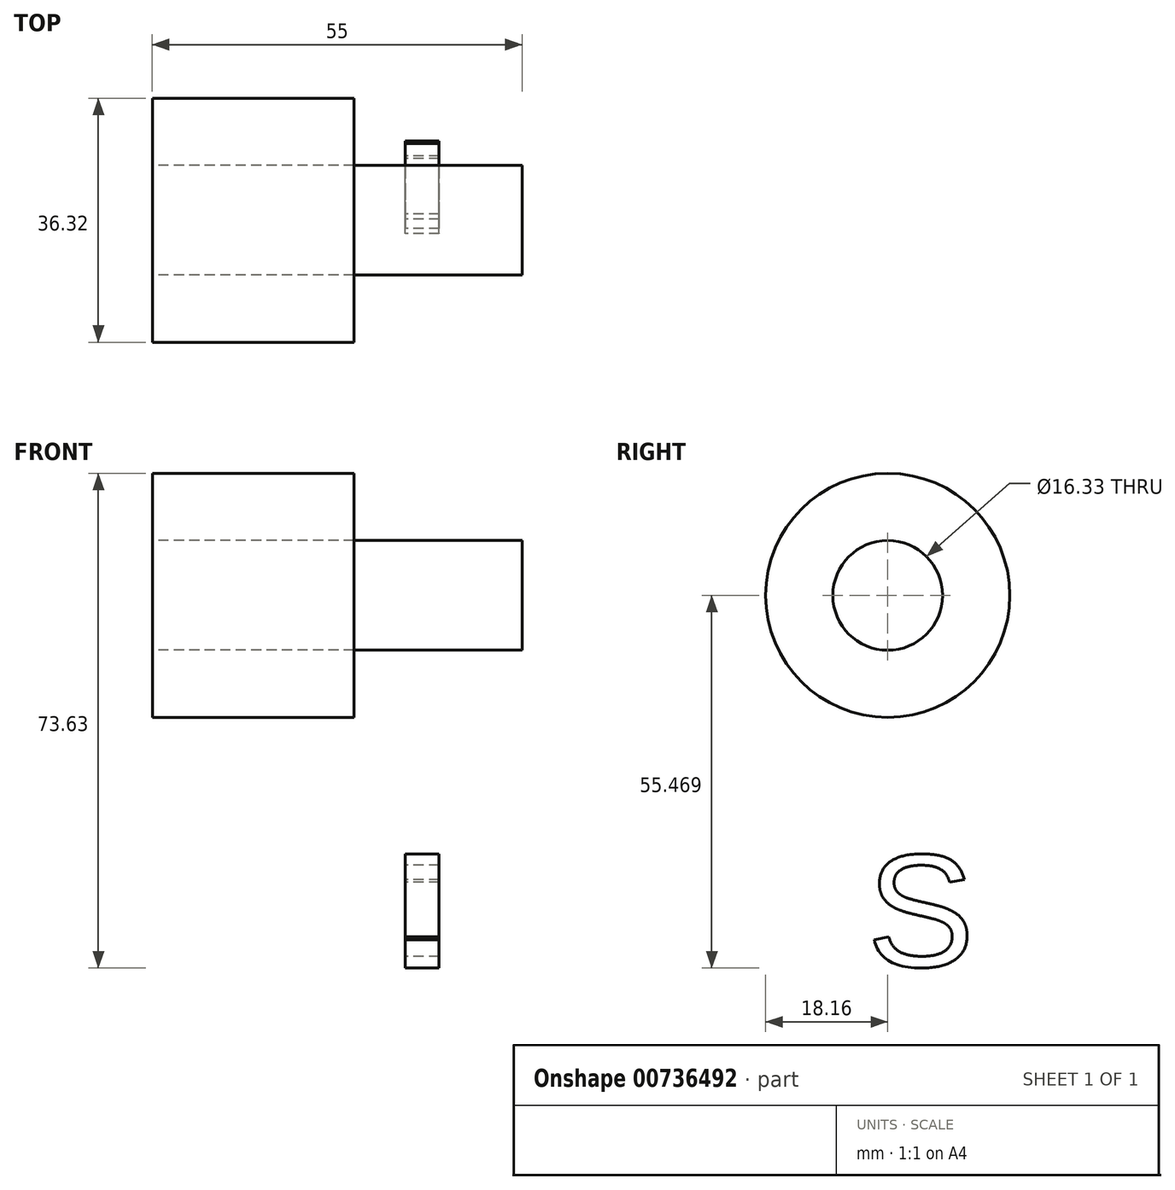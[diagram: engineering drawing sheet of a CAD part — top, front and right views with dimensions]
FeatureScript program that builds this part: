
annotation { "Feature Type Name" : "Feature", "Feature Type Description" : "" }
export const myFeature = defineFeature(function(context is Context, id is Id, definition is map)
    precondition{}
    {
        {
            var Q0;
            Q0=qCreatedBy(makeId("Front.planeOp"),FACE);
            var sketch = newSketch(context, id + "F0", { "sketchPlane" : qUnion([Q0])});
            skLineSegment(sketch, "E0.bottom", {"start": v(-37.65, 22.75) * mm, "end": v(-7.65, 22.75) * mm});
            skLineSegment(sketch, "E0.top", {"start": v(-37.65, 12.75) * mm, "end": v(-7.65, 12.75) * mm});
            skLineSegment(sketch, "E0.left", {"start": v(-37.65, 22.75) * mm, "end": v(-37.65, 12.75) * mm});
            skLineSegment(sketch, "E0.right", {"start": v(-7.65, 22.75) * mm, "end": v(-7.65, 12.75) * mm});
            skLineSegment(sketch, "E1", {"start": v(-37.75, 4.59) * mm, "end": v(-6.66, 4.59) * mm});
            skSolve(sketch);
        }
        {
            var Q0;
            Q0=makeQuery(id+"F0.imprint","IMPRINT",FACE,{"disambiguationData":[TD([[makeQuery(id+"F0.imprint","IMPRINT",EDGE,{"derivedFrom":sQuery(id+"F0.wireOp",EDGE,"E0.bottom")}),-1.0]])]});
            var Q1;
            Q1=sQuery(id+"F0.wireOp",EDGE,"E1");
            revolve(context, id + "F1", {"surfaceOperationType" : NewSurfaceOperationType.NEW, "entities" : qUnion([Q0]), "axis" : qUnion([Q1]), "revolveType" : RevolveType.FULL});
        }
        {
            var Q0;
            Q0=makeQuery(id+"F1.opRevolve","SWEPT_FACE",FACE,{"disambiguationData":[OSD([sQuery(id+"F0.wireOp",EDGE,"E0.right")])]});
            var sketch = newSketch(context, id + "F2", { "sketchPlane" : qUnion([Q0])});
            skCircle(sketch, "E2", {"center": v(0, 4.59) * mm, "radius": 8.37 * mm});
            skSolve(sketch);
        }
        {
            var Q0;
            Q0=makeQuery(id+"F2.imprint","IMPRINT",FACE,{"disambiguationData":[TD([[makeQuery(id+"F2.imprint","IMPRINT",EDGE,{"derivedFrom":makeQuery(id+"F1.opRevolve","SWEPT_EDGE",EDGE,{"disambiguationData":[OSD([sQuery(id+"F0.wireOp",EDGE,"E0.top"),sQuery(id+"F0.wireOp",EDGE,"E0.right")])]})}),-1.0]])]});
            extrude(context, id + "F3", {"entities" : qUnion([Q0]), "depth" : 25 * mm, "offsetDistance" : 25 * mm});
        }
        {
            var Q0;
            Q0=qCreatedBy(makeId("Right.planeOp"),FACE);
            var sketch = newSketch(context, id + "F4", { "sketchPlane" : qUnion([Q0])});
            skText(sketch, "E3", { "text": "S", "fontName": "Arimo-Regular.ttf"});
            const initialGuessF4  = {"E3": [-0.0031, -0.05064, 1, 0, 0.01728]};
            skSetInitialGuess(sketch, initialGuessF4);
            skSolve(sketch);
        }
        {
            var Q0;
            Q0 = qSketchRegion(id + "F4", true);
            extrude(context, id + "F5", {"entities" : qUnion([Q0]), "depth" : 5 * mm, "offsetDistance" : 25 * mm});
        }
    });
